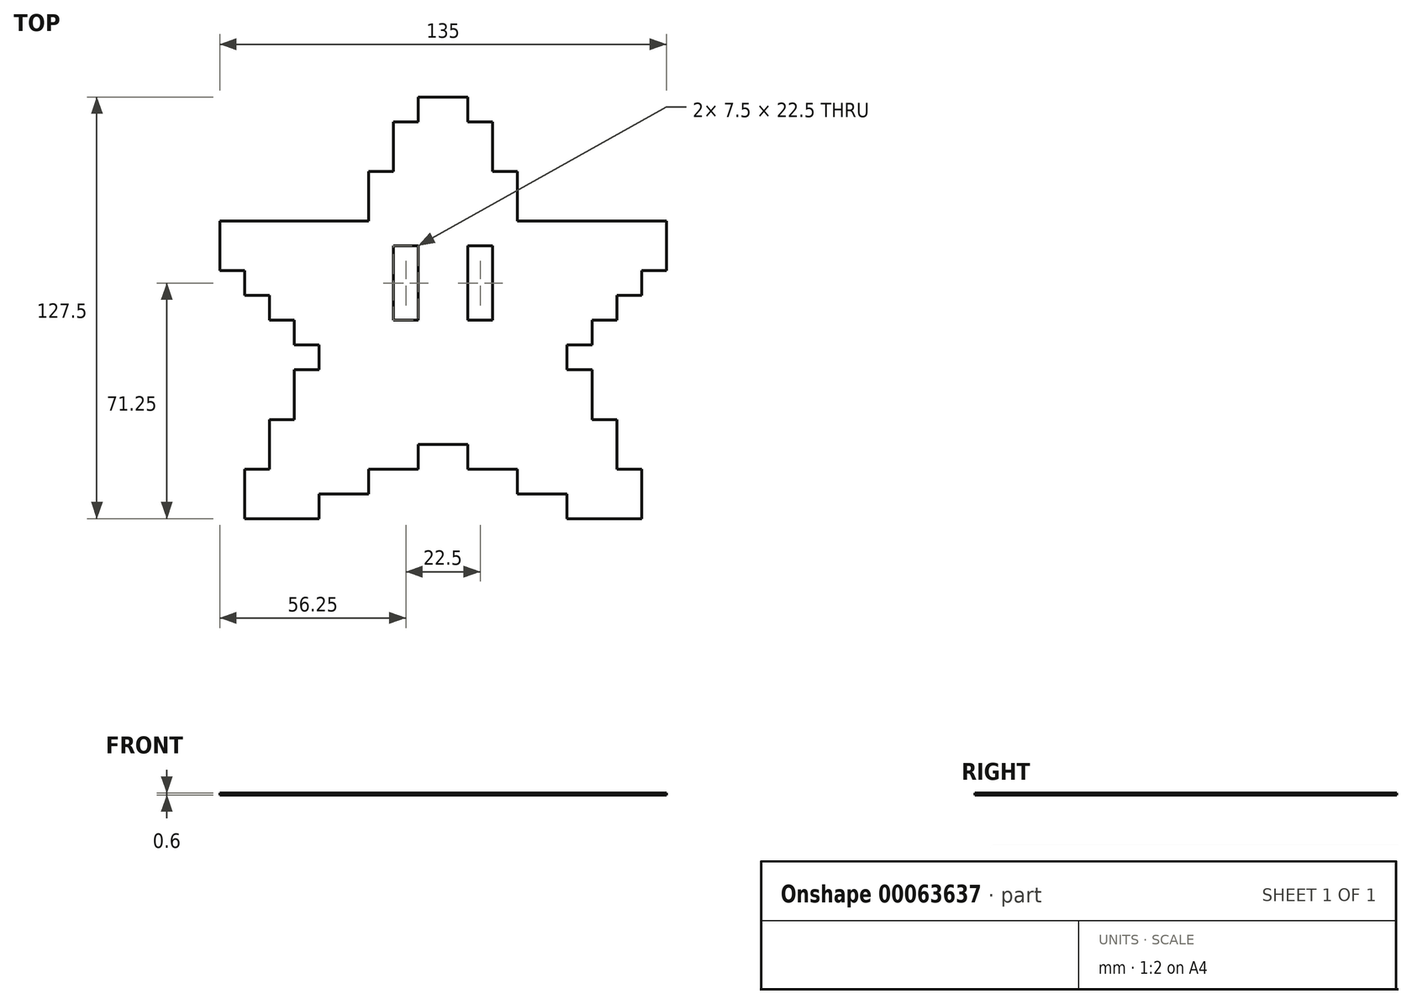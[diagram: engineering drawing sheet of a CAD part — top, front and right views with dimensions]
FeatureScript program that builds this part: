
annotation { "Feature Type Name" : "Feature", "Feature Type Description" : "" }
export const myFeature = defineFeature(function(context is Context, id is Id, definition is map)
    precondition{}
    {
        {
            var Q0;
            Q0=qCreatedBy(makeId("Top.planeOp"),FACE);
            var sketch = newSketch(context, id + "F0", { "sketchPlane" : qUnion([Q0])});
            skLineSegment(sketch, "E0", {"start": v(0, 37.5) * mm, "end": v(-7.5, 37.5) * mm});
            skLineSegment(sketch, "E1", {"start": v(-7.5, 37.5) * mm, "end": v(-7.5, 30) * mm});
            skLineSegment(sketch, "E2", {"start": v(-7.5, 30) * mm, "end": v(-15, 30) * mm});
            skLineSegment(sketch, "E3", {"start": v(-15, 30) * mm, "end": v(-15, 15) * mm});
            skLineSegment(sketch, "E4", {"start": v(-15, 15) * mm, "end": v(-22.5, 15) * mm});
            skLineSegment(sketch, "E5", {"start": v(-22.5, 15) * mm, "end": v(-22.5, 0) * mm});
            skLineSegment(sketch, "E6", {"start": v(-22.5, 0) * mm, "end": v(-67.5, 0) * mm});
            skLineSegment(sketch, "E7", {"start": v(-67.5, 0) * mm, "end": v(-67.5, -15) * mm});
            skLineSegment(sketch, "E8", {"start": v(-67.5, -15) * mm, "end": v(-60, -15) * mm});
            skLineSegment(sketch, "E9", {"start": v(-60, -15) * mm, "end": v(-60, -22.5) * mm});
            skLineSegment(sketch, "E10", {"start": v(-60, -22.5) * mm, "end": v(-52.5, -22.5) * mm});
            skLineSegment(sketch, "E11", {"start": v(-52.5, -22.5) * mm, "end": v(-52.5, -30) * mm});
            skLineSegment(sketch, "E12", {"start": v(-52.5, -30) * mm, "end": v(-45, -30) * mm});
            skLineSegment(sketch, "E13", {"start": v(-45, -30) * mm, "end": v(-45, -37.5) * mm});
            skLineSegment(sketch, "E14", {"start": v(-45, -37.5) * mm, "end": v(-37.5, -37.5) * mm});
            skLineSegment(sketch, "E15", {"start": v(-37.5, -37.5) * mm, "end": v(-37.5, -45) * mm});
            skLineSegment(sketch, "E16", {"start": v(-37.5, -45) * mm, "end": v(-45, -45) * mm});
            skLineSegment(sketch, "E17", {"start": v(-45, -45) * mm, "end": v(-45, -60) * mm});
            skLineSegment(sketch, "E18", {"start": v(-45, -60) * mm, "end": v(-52.5, -60) * mm});
            skLineSegment(sketch, "E19", {"start": v(-52.5, -60) * mm, "end": v(-52.5, -75) * mm});
            skLineSegment(sketch, "E20", {"start": v(-52.5, -75) * mm, "end": v(-60, -75) * mm});
            skLineSegment(sketch, "E21", {"start": v(-60, -75) * mm, "end": v(-60, -90) * mm});
            skLineSegment(sketch, "E22", {"start": v(-60, -90) * mm, "end": v(-37.5, -90) * mm});
            skLineSegment(sketch, "E23", {"start": v(-37.5, -90) * mm, "end": v(-37.5, -82.5) * mm});
            skLineSegment(sketch, "E24", {"start": v(-37.5, -82.5) * mm, "end": v(-22.5, -82.5) * mm});
            skLineSegment(sketch, "E25", {"start": v(-22.5, -82.5) * mm, "end": v(-22.5, -75) * mm});
            skLineSegment(sketch, "E26", {"start": v(-22.5, -75) * mm, "end": v(-7.5, -75) * mm});
            skLineSegment(sketch, "E27", {"start": v(-7.5, -75) * mm, "end": v(-7.5, -67.5) * mm});
            skLineSegment(sketch, "E28", {"start": v(-7.5, -67.5) * mm, "end": v(0, -67.5) * mm});
            skLineSegment(sketch, "E29.MirrorCS", {"start": v(45, -60) * mm, "end": v(52.5, -60) * mm});
            skLineSegment(sketch, "E30.MirrorCS", {"start": v(22.5, -75) * mm, "end": v(7.5, -75) * mm});
            skLineSegment(sketch, "E31.MirrorCS", {"start": v(52.5, -60) * mm, "end": v(52.5, -75) * mm});
            skLineSegment(sketch, "E32.MirrorCS", {"start": v(45, -30) * mm, "end": v(45, -37.5) * mm});
            skLineSegment(sketch, "E33.MirrorCS", {"start": v(45, -37.5) * mm, "end": v(37.5, -37.5) * mm});
            skLineSegment(sketch, "E34.MirrorCS", {"start": v(37.5, -37.5) * mm, "end": v(37.5, -45) * mm});
            skLineSegment(sketch, "E35.MirrorCS", {"start": v(0, 37.5) * mm, "end": v(7.5, 37.5) * mm});
            skLineSegment(sketch, "E36.MirrorCS", {"start": v(7.5, 37.5) * mm, "end": v(7.5, 30) * mm});
            skLineSegment(sketch, "E37.MirrorCS", {"start": v(7.5, 30) * mm, "end": v(15, 30) * mm});
            skLineSegment(sketch, "E38.MirrorCS", {"start": v(15, 30) * mm, "end": v(15, 15) * mm});
            skLineSegment(sketch, "E39.MirrorCS", {"start": v(15, 15) * mm, "end": v(22.5, 15) * mm});
            skLineSegment(sketch, "E40.MirrorCS", {"start": v(22.5, 15) * mm, "end": v(22.5, 0) * mm});
            skLineSegment(sketch, "E41.MirrorCS", {"start": v(22.5, 0) * mm, "end": v(67.5, 0) * mm});
            skLineSegment(sketch, "E42.MirrorCS", {"start": v(67.5, 0) * mm, "end": v(67.5, -15) * mm});
            skLineSegment(sketch, "E43.MirrorCS", {"start": v(67.5, -15) * mm, "end": v(60, -15) * mm});
            skLineSegment(sketch, "E44.MirrorCS", {"start": v(60, -15) * mm, "end": v(60, -22.5) * mm});
            skLineSegment(sketch, "E45.MirrorCS", {"start": v(60, -22.5) * mm, "end": v(52.5, -22.5) * mm});
            skLineSegment(sketch, "E46.MirrorCS", {"start": v(52.5, -22.5) * mm, "end": v(52.5, -30) * mm});
            skLineSegment(sketch, "E47.MirrorCS", {"start": v(52.5, -30) * mm, "end": v(45, -30) * mm});
            skLineSegment(sketch, "E48.MirrorCS", {"start": v(7.5, -75) * mm, "end": v(7.5, -67.5) * mm});
            skLineSegment(sketch, "E49.MirrorCS", {"start": v(37.5, -90) * mm, "end": v(37.5, -82.5) * mm});
            skLineSegment(sketch, "E50.MirrorCS", {"start": v(52.5, -75) * mm, "end": v(60, -75) * mm});
            skLineSegment(sketch, "E51.MirrorCS", {"start": v(37.5, -45) * mm, "end": v(45, -45) * mm});
            skLineSegment(sketch, "E52.MirrorCS", {"start": v(7.5, -67.5) * mm, "end": v(0, -67.5) * mm});
            skLineSegment(sketch, "E53.MirrorCS", {"start": v(37.5, -82.5) * mm, "end": v(22.5, -82.5) * mm});
            skLineSegment(sketch, "E54.MirrorCS", {"start": v(60, -75) * mm, "end": v(60, -90) * mm});
            skLineSegment(sketch, "E55.MirrorCS", {"start": v(45, -45) * mm, "end": v(45, -60) * mm});
            skLineSegment(sketch, "E56.MirrorCS", {"start": v(22.5, -82.5) * mm, "end": v(22.5, -75) * mm});
            skLineSegment(sketch, "E57.MirrorCS", {"start": v(60, -90) * mm, "end": v(37.5, -90) * mm});
            skLineSegment(sketch, "E58.bottom", {"start": v(-15, -7.5) * mm, "end": v(-7.5, -7.5) * mm});
            skLineSegment(sketch, "E58.top", {"start": v(-15, -30) * mm, "end": v(-7.5, -30) * mm});
            skLineSegment(sketch, "E58.left", {"start": v(-15, -7.5) * mm, "end": v(-15, -30) * mm});
            skLineSegment(sketch, "E58.right", {"start": v(-7.5, -7.5) * mm, "end": v(-7.5, -30) * mm});
            skLineSegment(sketch, "E59.MirrorCS", {"start": v(15, -30) * mm, "end": v(7.5, -30) * mm});
            skLineSegment(sketch, "E60.MirrorCS", {"start": v(15, -7.5) * mm, "end": v(15, -30) * mm});
            skLineSegment(sketch, "E61.MirrorCS", {"start": v(15, -7.5) * mm, "end": v(7.5, -7.5) * mm});
            skLineSegment(sketch, "E62.MirrorCS", {"start": v(7.5, -7.5) * mm, "end": v(7.5, -30) * mm});
            skSolve(sketch);
        }
        {
            var Q0;
            Q0=makeQuery(id+"F0.imprint","IMPRINT",FACE,{"disambiguationData":[TD([[makeQuery(id+"F0.imprint","IMPRINT",EDGE,{"derivedFrom":sQuery(id+"F0.wireOp",EDGE,"E0")}),1.0]])]});
            extrude(context, id + "F1", {"entities" : qUnion([Q0]), "depth" : 0.6 * mm});
        }
    });
